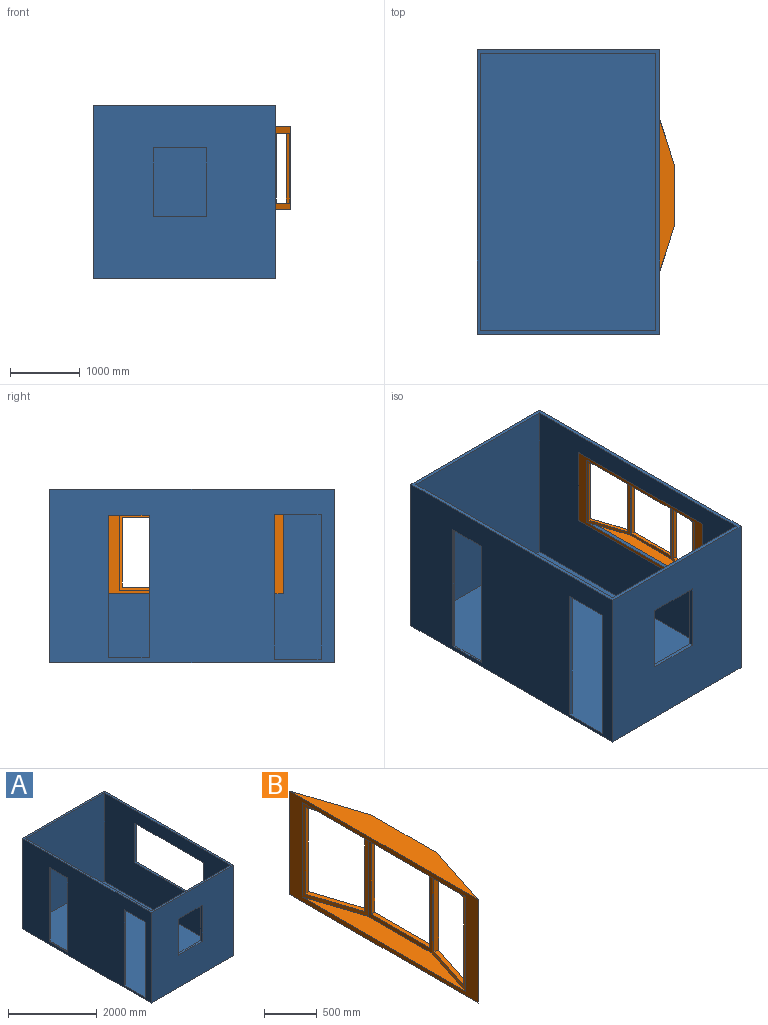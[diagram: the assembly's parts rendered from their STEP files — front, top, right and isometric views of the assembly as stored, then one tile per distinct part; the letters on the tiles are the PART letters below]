
ASSEMBLY  parts=2 mates=1
PART A: 30 faces, bbox 2616.2x4089.4x2489.2 mm
  f0: plane 2044.7x25.4mm, normal (0,-1,0), area 51935.4mm2, adj f1,f3,f4,f29
  f1: plane 584.2x25.4mm, normal (0,0,-1), area 14838.7mm2, adj f0,f2,f4,f29
  f2: plane 2044.7x25.4mm, normal (0,1,0), area 51935.4mm2, adj f1,f3,f4,f29
  f3: plane 584.2x25.4mm, normal (0,0,1), area 14838.7mm2, adj f0,f2,f4,f29
  f4: plane 4089.4x2489.2mm, normal (-1,0,0), area 7582888.1mm2, adj f0,f1,f2,f3,f6,f10,f11,f12
  f5: plane 3987.8x2438.4mm, normal (1,0,0), area 7025792.4mm2, adj f7,f10,f13,f14,f23,f24,f25,f26
  f6: plane 2616.2x2489.2mm, normal (0,-1,0), area 5757407.8mm2, adj f4,f8,f10,f12,f19,f20,f21,f22
  f7: plane 2514.6x2438.4mm, normal (0,1,0), area 5376763.4mm2, adj f5,f9,f10,f14,f19,f20,f21,f22
  f8: plane 4089.4x2489.2mm, normal (1,0,0), area 7793532.8mm2, adj f6,f10,f11,f12,f15,f16,f17,f18
  f9: plane 3987.8x2438.4mm, normal (-1,0,0), area 7338049.8mm2, adj f7,f10,f13,f14,f15,f16,f17,f18
  f10: plane 4089.4x2616.2mm, normal (0,0,1), area 670966.4mm2, adj f4,f5,f6,f7,f8,f9,f11,f13
  f11: plane 2616.2x2489.2mm, normal (0,1,0), area 6512245mm2, adj f4,f8,f10,f12
  f12: plane 4089.4x2616.2mm, normal (0,0,-1), area 10698688.3mm2, adj f4,f6,f8,f11
  f13: plane 2514.6x2438.4mm, normal (0,-1,0), area 6131600.6mm2, adj f5,f9,f10,f14
  f14: plane 3987.8x2565.4mm, normal (0,0,1), area 10077721.8mm2, adj f4,f5,f7,f9,f13,f23,f24,f26
  f15: plane 1092.2x50.8mm, normal (0,-1,0), area 55483.8mm2, adj f8,f9,f16,f18
  f16: plane 2184.4x50.8mm, normal (0,0,1), area 110967.5mm2, adj f8,f9,f15,f17
  f17: plane 1092.2x50.8mm, normal (0,1,0), area 55483.8mm2, adj f8,f9,f16,f18
  f18: plane 2184.4x50.8mm, normal (0,0,-1), area 110967.5mm2, adj f8,f9,f15,f17
  f19: plane 990.6x50.8mm, normal (-1,0,0), area 50322.5mm2, adj f6,f7,f20,f22
  f20: plane 762x50.8mm, normal (0,0,1), area 38709.6mm2, adj f6,f7,f19,f21
  f21: plane 990.6x50.8mm, normal (1,0,0), area 50322.5mm2, adj f6,f7,f20,f22
  f22: plane 762x50.8mm, normal (0,0,-1), area 38709.6mm2, adj f6,f7,f19,f21
  f23: plane 2082.8x50.8mm, normal (0,1,0), area 105806.2mm2, adj f4,f5,f14,f25
  f24: plane 2082.8x50.8mm, normal (0,-1,0), area 105806.2mm2, adj f4,f5,f14,f25
  f25: plane 673.1x50.8mm, normal (0,0,-1), area 34193.5mm2, adj f4,f5,f23,f24
  f26: plane 2082.8x25.4mm, normal (0,1,0), area 52903.1mm2, adj f5,f14,f28,f29
  f27: plane 2082.8x25.4mm, normal (0,-1,0), area 52903.1mm2, adj f5,f14,f28,f29
  f28: plane 622.3x25.4mm, normal (0,0,-1), area 15806.4mm2, adj f5,f26,f27,f29
  f29: plane 2082.8x622.3mm, normal (1,0,0), area 101612.7mm2, adj f0,f1,f2,f3,f14,f26,f27,f28
PART B: 23 faces, bbox 266.7x2514.2x1193.8 mm
  f0: plane 1193.8x823.63mm, normal (0.95,-0.31,0), area 406820.5mm2, adj f2,f3,f4,f5,f15,f16,f17,f18
  f1: plane 1092.2x666.75mm, normal (-0.95,0.31,0), area 138755.6mm2, adj f3,f7,f8,f9,f15,f16,f17,f18
  f2: plane 1193.8x866.94mm, normal (1,0,0), area 257695.9mm2, adj f0,f4,f5,f6,f11,f12,f13,f14
  f3: plane 2514.2x1193.8mm, normal (-1,0,0), area 615655.4mm2, adj f0,f1,f4,f5,f6,f7,f9,f10
  f4: plane 2514.2x266.7mm, normal (0,0,1), area 450875.5mm2, adj f0,f2,f3,f6
  f5: plane 2514.2x266.7mm, normal (0,0,-1), area 450875.5mm2, adj f0,f2,f3,f6
  f6: plane 1193.8x823.63mm, normal (0.95,0.31,0), area 406820.5mm2, adj f2,f3,f4,f5,f19,f20,f21,f22
  f7: plane 2184.4x215.9mm, normal (0,0,-1), area 327660.6mm2, adj f1,f3,f8,f10
  f8: plane 1092.2x850.9mm, normal (-1,0,0), area 152096.5mm2, adj f1,f7,f9,f10,f11,f12,f13,f14
  f9: plane 2184.4x215.9mm, normal (0,0,1), area 327660.6mm2, adj f1,f3,f8,f10
  f10: plane 1092.2x666.75mm, normal (-0.95,-0.31,0), area 138755.6mm2, adj f3,f7,f8,f9,f19,f20,f21,f22
  f11: plane 774.7x50.8mm, normal (0,0,1), area 39354.8mm2, adj f2,f8,f12,f14
  f12: plane 1003.3x50.8mm, normal (0,1,0), area 50967.6mm2, adj f2,f8,f11,f13
  f13: plane 774.7x50.8mm, normal (0,0,-1), area 39354.8mm2, adj f2,f8,f12,f14
  f14: plane 1003.3x50.8mm, normal (0,-1,0), area 50967.6mm2, adj f2,f8,f11,f13
  f15: plane 609.91x240.76mm, normal (0,0,-1), area 31731.4mm2, adj f0,f1,f16,f18
  f16: plane 1003.3x48.33mm, normal (-0.31,-0.95,0), area 50967.6mm2, adj f0,f1,f15,f17
  f17: plane 609.91x240.76mm, normal (0,0,1), area 31731.4mm2, adj f0,f1,f16,f18
  f18: plane 1003.3x48.33mm, normal (0.31,0.95,0), area 50967.6mm2, adj f0,f1,f15,f17
  f19: plane 1003.3x48.33mm, normal (0.31,-0.95,0), area 50967.6mm2, adj f6,f10,f20,f22
  f20: plane 609.91x240.76mm, normal (0,0,1), area 31731.4mm2, adj f6,f10,f19,f21
  f21: plane 1003.3x48.33mm, normal (-0.31,0.95,0), area 50967.6mm2, adj f6,f10,f20,f22
  f22: plane 609.91x240.76mm, normal (0,0,-1), area 31731.4mm2, adj f6,f10,f19,f21
PLACE A at identity
PLACE B t=(1414.74,-1015.76,990.6)mm
MATE fastened B.f3 <-> A.f9  axis (-1,0,0) through (1414.74,76.44,2082.8)mm
